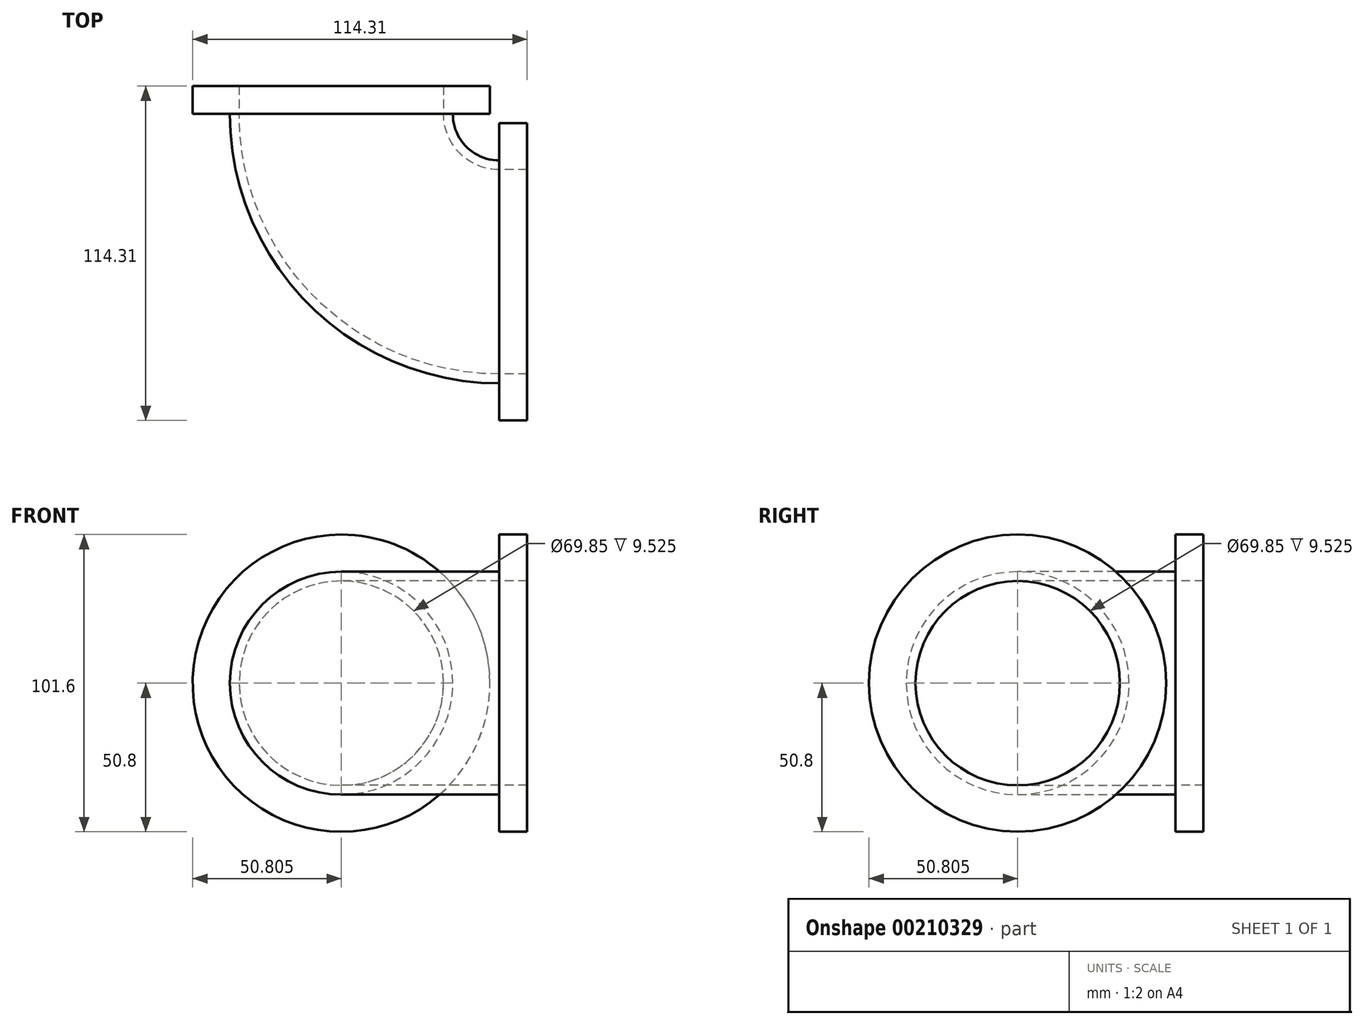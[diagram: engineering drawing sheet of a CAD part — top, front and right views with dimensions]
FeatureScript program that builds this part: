
annotation { "Feature Type Name" : "Feature", "Feature Type Description" : "" }
export const myFeature = defineFeature(function(context is Context, id is Id, definition is map)
    precondition{}
    {
        {
            var Q0;
            Q0=qCreatedBy(makeId("Front.planeOp"),FACE);
            var sketch = newSketch(context, id + "F0", { "sketchPlane" : qUnion([Q0])});
            skCircle(sketch, "E0", {"center": v(-53.98, 0) * mm, "radius": 38.1 * mm});
            skCircle(sketch, "E1", {"center": v(-53.98, 0) * mm, "radius": 34.93 * mm});
            skLineSegment(sketch, "E2", {"start": v(0, 0) * mm, "end": v(0, 54.16) * mm, "construction": true});
            skSolve(sketch);
        }
        {
            var Q0;
            Q0=makeQuery(id+"F0.imprint","IMPRINT",FACE,{"disambiguationData":[TD([[makeQuery(id+"F0.imprint","IMPRINT",EDGE,{"derivedFrom":sQuery(id+"F0.wireOp",EDGE,"E0")}),1.0]])]});
            var Q1;
            Q1=sQuery(id+"F0.wireOp",EDGE,"E2");
            revolve(context, id + "F1", {"entities" : qUnion([Q0]), "axis" : qUnion([Q1]), "revolveType" : RevolveType.ONE_DIRECTION, "angle" : 90 * degree});
        }
        {
            var Q0;
            Q0=makeQuery(id+"F1.opRevolve","CAP_FACE",FACE,{"disambiguationData":[OSD([sQuery(id+"F0.wireOp",EDGE,"E0"),sQuery(id+"F0.wireOp",EDGE,"E1")])],"isStart":false});
            var sketch = newSketch(context, id + "F2", { "sketchPlane" : qUnion([Q0])});
            skCircle(sketch, "E3", {"center": v(-53.98, 0) * mm, "radius": 50.8 * mm});
            skCircle(sketch, "E4", {"center": v(-53.98, 0) * mm, "radius": 34.93 * mm});
            skSolve(sketch);
        }
        {
            var Q0;
            Q0 = qSketchRegion(id + "F2", true);
            extrude(context, id + "F3", {"entities" : qUnion([Q0]), "operationType" : NewBodyOperationType.ADD, "depth" : 9.52 * mm});
        }
        {
            var Q0;
            Q0=makeQuery(id+"F1.opRevolve","CAP_FACE",FACE,{"disambiguationData":[OSD([sQuery(id+"F0.wireOp",EDGE,"E0"),sQuery(id+"F0.wireOp",EDGE,"E1")])],"isStart":true});
            var sketch = newSketch(context, id + "F4", { "sketchPlane" : qUnion([Q0])});
            skCircle(sketch, "E5", {"center": v(53.98, 0) * mm, "radius": 50.8 * mm});
            skCircle(sketch, "E6", {"center": v(53.98, 0) * mm, "radius": 34.93 * mm});
            skSolve(sketch);
        }
        {
            var Q0;
            Q0 = qSketchRegion(id + "F4", true);
            extrude(context, id + "F5", {"entities" : qUnion([Q0]), "operationType" : NewBodyOperationType.ADD, "depth" : 9.52 * mm});
        }
    });
